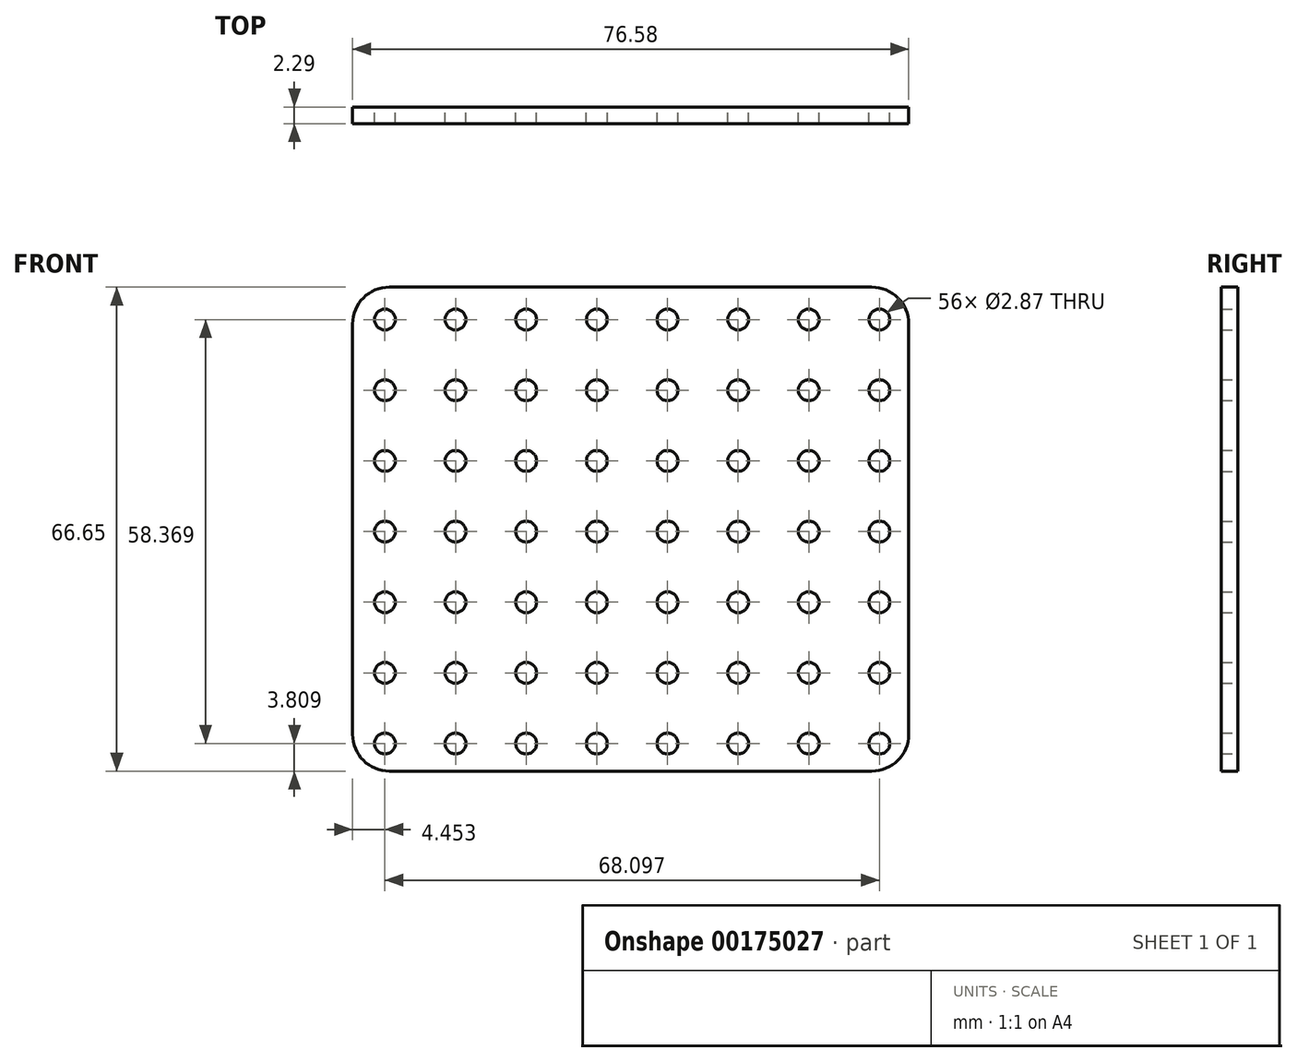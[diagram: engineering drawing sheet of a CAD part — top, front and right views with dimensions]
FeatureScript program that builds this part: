
annotation { "Feature Type Name" : "Feature", "Feature Type Description" : "" }
export const myFeature = defineFeature(function(context is Context, id is Id, definition is map)
    precondition{}
    {
        {
            var Q0;
            Q0=qCreatedBy(makeId("Front.planeOp"),FACE);
            var sketch = newSketch(context, id + "F0", { "sketchPlane" : qUnion([Q0])});
            skLineSegment(sketch, "E0.bottom", {"start": v(-40.67, 43.83) * mm, "end": v(35.9, 43.83) * mm});
            skLineSegment(sketch, "E0.top", {"start": v(-40.67, -22.82) * mm, "end": v(35.9, -22.82) * mm});
            skLineSegment(sketch, "E0.left", {"start": v(-40.67, 43.83) * mm, "end": v(-40.67, -22.82) * mm});
            skLineSegment(sketch, "E0.right", {"start": v(35.9, 43.83) * mm, "end": v(35.9, -22.82) * mm});
            skSolve(sketch);
        }
        {
            var Q0;
            Q0 = qSketchRegion(id + "F0", true);
            extrude(context, id + "F1", {"entities" : qUnion([Q0]), "depth" : 2.3 * mm});
        }
        {
            var Q0;
            Q0=qCreatedBy(makeId("Front.planeOp"),FACE);
            var sketch = newSketch(context, id + "F2", { "sketchPlane" : qUnion([Q0])});
            skCircle(sketch, "E1", {"center": v(-36.22, 39.36) * mm, "radius": 1.44 * mm});
            skCircle(sketch, "E2.0.1.0", {"center": v(-36.22, 29.63) * mm, "radius": 1.44 * mm});
            skCircle(sketch, "E2.0.2.0", {"center": v(-36.22, 19.9) * mm, "radius": 1.44 * mm});
            skCircle(sketch, "E2.0.3.0", {"center": v(-36.22, 10.17) * mm, "radius": 1.44 * mm});
            skCircle(sketch, "E2.0.4.0", {"center": v(-36.22, 0.45) * mm, "radius": 1.44 * mm});
            skCircle(sketch, "E2.0.5.0", {"center": v(-36.22, -9.28) * mm, "radius": 1.44 * mm});
            skCircle(sketch, "E2.0.6.0", {"center": v(-36.22, -19.01) * mm, "radius": 1.44 * mm});
            skCircle(sketch, "E2.1.0.0", {"center": v(-26.49, 39.36) * mm, "radius": 1.44 * mm});
            skCircle(sketch, "E2.1.1.0", {"center": v(-26.49, 29.63) * mm, "radius": 1.44 * mm});
            skCircle(sketch, "E2.1.2.0", {"center": v(-26.49, 19.9) * mm, "radius": 1.44 * mm});
            skCircle(sketch, "E2.1.3.0", {"center": v(-26.49, 10.17) * mm, "radius": 1.44 * mm});
            skCircle(sketch, "E2.1.4.0", {"center": v(-26.49, 0.45) * mm, "radius": 1.44 * mm});
            skCircle(sketch, "E2.1.5.0", {"center": v(-26.49, -9.28) * mm, "radius": 1.44 * mm});
            skCircle(sketch, "E2.1.6.0", {"center": v(-26.49, -19.01) * mm, "radius": 1.44 * mm});
            skCircle(sketch, "E2.2.0.0", {"center": v(-16.76, 39.36) * mm, "radius": 1.44 * mm});
            skCircle(sketch, "E2.2.1.0", {"center": v(-16.76, 29.63) * mm, "radius": 1.44 * mm});
            skCircle(sketch, "E2.2.2.0", {"center": v(-16.76, 19.9) * mm, "radius": 1.44 * mm});
            skCircle(sketch, "E2.2.3.0", {"center": v(-16.76, 10.17) * mm, "radius": 1.44 * mm});
            skCircle(sketch, "E2.2.4.0", {"center": v(-16.76, 0.45) * mm, "radius": 1.44 * mm});
            skCircle(sketch, "E2.2.5.0", {"center": v(-16.76, -9.28) * mm, "radius": 1.44 * mm});
            skCircle(sketch, "E2.2.6.0", {"center": v(-16.76, -19.01) * mm, "radius": 1.44 * mm});
            skCircle(sketch, "E2.3.0.0", {"center": v(-7.03, 39.36) * mm, "radius": 1.44 * mm});
            skCircle(sketch, "E2.3.1.0", {"center": v(-7.03, 29.63) * mm, "radius": 1.44 * mm});
            skCircle(sketch, "E2.3.2.0", {"center": v(-7.03, 19.9) * mm, "radius": 1.44 * mm});
            skCircle(sketch, "E2.3.3.0", {"center": v(-7.03, 10.17) * mm, "radius": 1.44 * mm});
            skCircle(sketch, "E2.3.4.0", {"center": v(-7.03, 0.45) * mm, "radius": 1.44 * mm});
            skCircle(sketch, "E2.3.5.0", {"center": v(-7.03, -9.28) * mm, "radius": 1.44 * mm});
            skCircle(sketch, "E2.3.6.0", {"center": v(-7.03, -19.01) * mm, "radius": 1.44 * mm});
            skCircle(sketch, "E2.4.0.0", {"center": v(2.7, 39.36) * mm, "radius": 1.44 * mm});
            skCircle(sketch, "E2.4.1.0", {"center": v(2.7, 29.63) * mm, "radius": 1.44 * mm});
            skCircle(sketch, "E2.4.2.0", {"center": v(2.7, 19.9) * mm, "radius": 1.44 * mm});
            skCircle(sketch, "E2.4.3.0", {"center": v(2.7, 10.17) * mm, "radius": 1.44 * mm});
            skCircle(sketch, "E2.4.4.0", {"center": v(2.7, 0.45) * mm, "radius": 1.44 * mm});
            skCircle(sketch, "E2.4.5.0", {"center": v(2.7, -9.28) * mm, "radius": 1.44 * mm});
            skCircle(sketch, "E2.4.6.0", {"center": v(2.7, -19.01) * mm, "radius": 1.44 * mm});
            skCircle(sketch, "E2.5.0.0", {"center": v(12.42, 39.36) * mm, "radius": 1.44 * mm});
            skCircle(sketch, "E2.5.1.0", {"center": v(12.42, 29.63) * mm, "radius": 1.44 * mm});
            skCircle(sketch, "E2.5.2.0", {"center": v(12.42, 19.9) * mm, "radius": 1.44 * mm});
            skCircle(sketch, "E2.5.3.0", {"center": v(12.42, 10.17) * mm, "radius": 1.44 * mm});
            skCircle(sketch, "E2.5.4.0", {"center": v(12.42, 0.45) * mm, "radius": 1.44 * mm});
            skCircle(sketch, "E2.5.5.0", {"center": v(12.42, -9.28) * mm, "radius": 1.44 * mm});
            skCircle(sketch, "E2.5.6.0", {"center": v(12.42, -19.01) * mm, "radius": 1.44 * mm});
            skCircle(sketch, "E2.6.0.0", {"center": v(22.15, 39.36) * mm, "radius": 1.44 * mm});
            skCircle(sketch, "E2.6.1.0", {"center": v(22.15, 29.63) * mm, "radius": 1.44 * mm});
            skCircle(sketch, "E2.6.2.0", {"center": v(22.15, 19.9) * mm, "radius": 1.44 * mm});
            skCircle(sketch, "E2.6.3.0", {"center": v(22.15, 10.17) * mm, "radius": 1.44 * mm});
            skCircle(sketch, "E2.6.4.0", {"center": v(22.15, 0.45) * mm, "radius": 1.44 * mm});
            skCircle(sketch, "E2.6.5.0", {"center": v(22.15, -9.28) * mm, "radius": 1.44 * mm});
            skCircle(sketch, "E2.6.6.0", {"center": v(22.15, -19.01) * mm, "radius": 1.44 * mm});
            skCircle(sketch, "E2.7.0.0", {"center": v(31.88, 39.36) * mm, "radius": 1.44 * mm});
            skCircle(sketch, "E2.7.1.0", {"center": v(31.88, 29.63) * mm, "radius": 1.44 * mm});
            skCircle(sketch, "E2.7.2.0", {"center": v(31.88, 19.9) * mm, "radius": 1.44 * mm});
            skCircle(sketch, "E2.7.3.0", {"center": v(31.88, 10.17) * mm, "radius": 1.44 * mm});
            skCircle(sketch, "E2.7.4.0", {"center": v(31.88, 0.45) * mm, "radius": 1.44 * mm});
            skCircle(sketch, "E2.7.5.0", {"center": v(31.88, -9.28) * mm, "radius": 1.44 * mm});
            skCircle(sketch, "E2.7.6.0", {"center": v(31.88, -19.01) * mm, "radius": 1.44 * mm});
            skLineSegment(sketch, "E2.direction1", {"start": v(-36.22, 39.36) * mm, "end": v(-26.49, 39.36) * mm, "construction": true});
            skLineSegment(sketch, "E2.direction2", {"start": v(-36.22, 39.36) * mm, "end": v(-36.22, 29.63) * mm, "construction": true});
            skSolve(sketch);
        }
        {
            var Q0;
            Q0 = qSketchRegion(id + "F2", true);
            extrude(context, id + "F3", {"entities" : qUnion([Q0]), "operationType" : NewBodyOperationType.REMOVE, "depth" : 2.3 * mm});
        }
        {
            var Q0;
            Q0=makeQuery(id+"F1.opExtrude","SWEPT_EDGE",EDGE,{"disambiguationData":[OSD([sQuery(id+"F0.wireOp",EDGE,"E0.top"),sQuery(id+"F0.wireOp",EDGE,"E0.left")])]});
            var Q1;
            Q1=makeQuery(id+"F1.opExtrude","SWEPT_EDGE",EDGE,{"disambiguationData":[OSD([sQuery(id+"F0.wireOp",EDGE,"E0.bottom"),sQuery(id+"F0.wireOp",EDGE,"E0.right")])]});
            var Q2;
            Q2=makeQuery(id+"F1.opExtrude","SWEPT_EDGE",EDGE,{"disambiguationData":[OSD([sQuery(id+"F0.wireOp",EDGE,"E0.top"),sQuery(id+"F0.wireOp",EDGE,"E0.right")])]});
            var Q3;
            Q3=makeQuery(id+"F1.opExtrude","SWEPT_EDGE",EDGE,{"disambiguationData":[OSD([sQuery(id+"F0.wireOp",EDGE,"E0.bottom"),sQuery(id+"F0.wireOp",EDGE,"E0.left")])]});
            fillet(context, id + "F4", {"entities" : qUnion([Q0, Q1, Q2, Q3]), "radius" : 5.08 * mm, "tangentPropagation" : true, "allowEdgeOverflow" : false});
        }
    });
